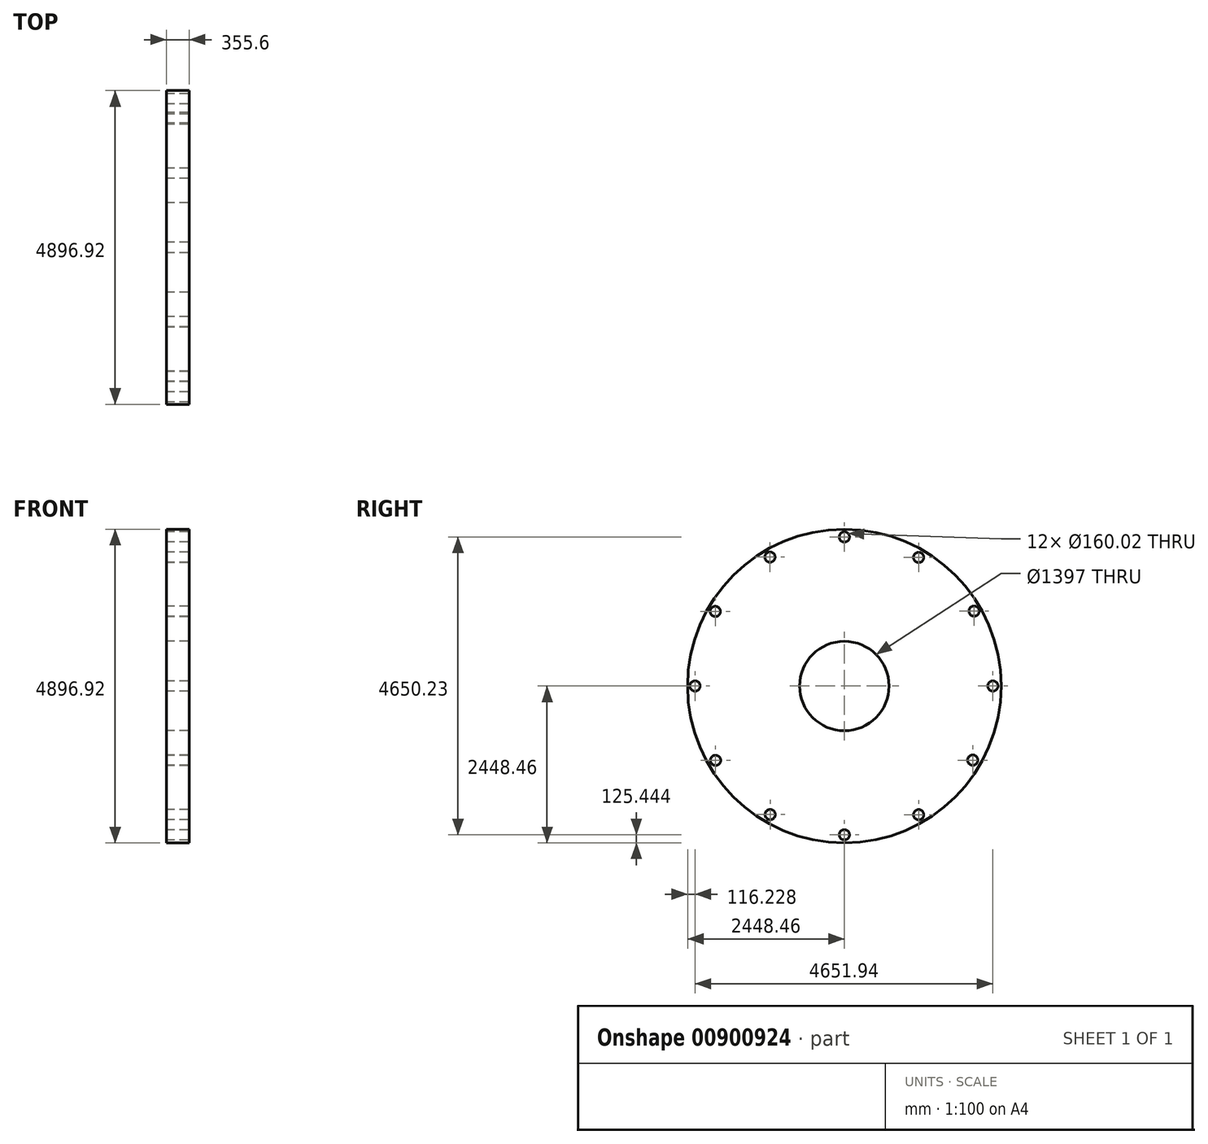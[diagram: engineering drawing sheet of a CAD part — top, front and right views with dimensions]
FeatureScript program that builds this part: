
annotation { "Feature Type Name" : "Feature", "Feature Type Description" : "" }
export const myFeature = defineFeature(function(context is Context, id is Id, definition is map)
    precondition{}
    {
        {
            var Q0;
            Q0=qCreatedBy(makeId("Right.planeOp"),FACE);
            var sketch = newSketch(context, id + "F0", { "sketchPlane" : qUnion([Q0])});
            skCircle(sketch, "E0", {"center": v(0, 0) * mm, "radius": 2448.46 * mm});
            skCircle(sketch, "E1", {"center": v(0, 0) * mm, "radius": 2192.02 * mm});
            skCircle(sketch, "E2", {"center": v(0, 2327.22) * mm, "radius": 80 * mm});
            skCircle(sketch, "E3", {"center": v(1159.34, 2008.04) * mm, "radius": 80.01 * mm});
            skCircle(sketch, "E4", {"center": v(2025.62, 1169.5) * mm, "radius": 80.01 * mm});
            skCircle(sketch, "E5", {"center": v(2319.7, 0) * mm, "radius": 80.01 * mm});
            skCircle(sketch, "E6", {"center": v(2003.89, -1156.94) * mm, "radius": 80.01 * mm});
            skCircle(sketch, "E7", {"center": v(1160.2, -2009.53) * mm, "radius": 80.01 * mm});
            skCircle(sketch, "E8", {"center": v(0, -2323.02) * mm, "radius": 80.01 * mm});
            skCircle(sketch, "E9", {"center": v(-1159.13, -2007.66) * mm, "radius": 80.01 * mm});
            skCircle(sketch, "E10", {"center": v(-2010.64, -1160.84) * mm, "radius": 80.01 * mm});
            skCircle(sketch, "E11", {"center": v(-2332.23, 0) * mm, "radius": 80.01 * mm});
            skCircle(sketch, "E12", {"center": v(-2016.43, 1164.19) * mm, "radius": 80.01 * mm});
            skCircle(sketch, "E13", {"center": v(-1162.2, 2013) * mm, "radius": 80.01 * mm});
            skCircle(sketch, "E14", {"center": v(0, 0) * mm, "radius": 762 * mm});
            skCircle(sketch, "E15", {"center": v(0, 0) * mm, "radius": 698.5 * mm});
            skCircle(sketch, "E16", {"center": v(0, 0) * mm, "radius": 869.06 * mm});
            skLineSegment(sketch, "E17", {"start": v(447.49, 616.76) * mm, "end": v(502.9, 708.78) * mm});
            skSolve(sketch);
        }
        {
            var Q0;
            Q0=makeQuery(id+"F0.imprint","IMPRINT",FACE,{"disambiguationData":[TD([[makeQuery(id+"F0.imprint","IMPRINT",EDGE,{"derivedFrom":sQuery(id+"F0.wireOp",EDGE,"E0")}),1.0]])]});
            var Q1;
            Q1=makeQuery(id+"F0.imprint","IMPRINT",FACE,{"disambiguationData":[TD([[makeQuery(id+"F0.imprint","IMPRINT",EDGE,{"derivedFrom":sQuery(id+"F0.wireOp",EDGE,"E14")}),1.0]])]});
            var Q2;
            Q2=makeQuery(id+"F0.imprint","IMPRINT",FACE,{"disambiguationData":[TD([[makeQuery(id+"F0.imprint","IMPRINT",EDGE,{"derivedFrom":sQuery(id+"F0.wireOp",EDGE,"305all4X-0Ig5-pPF4-IkFr-XuM0qsScPcYt")}),1.0]])]});
            var Q3;
            Q3=makeQuery(id+"F0.imprint","IMPRINT",FACE,{"disambiguationData":[TD([[makeQuery(id+"F0.imprint","IMPRINT",EDGE,{"derivedFrom":sQuery(id+"F0.wireOp",EDGE,"E1")}),1.0]])]});
            var Q4;
            Q4=makeQuery(id+"F0.imprint","IMPRINT",FACE,{"disambiguationData":[TD([[makeQuery(id+"F0.imprint","IMPRINT",EDGE,{"derivedFrom":sQuery(id+"F0.wireOp",EDGE,"E14")}),-1.0]])]});
            extrude(context, id + "F1", {"entities" : qUnion([Q0, Q1, Q2, Q3, Q4]), "depth" : 355.6 * mm, "offsetDistance" : 25.4 * mm});
        }
    });
